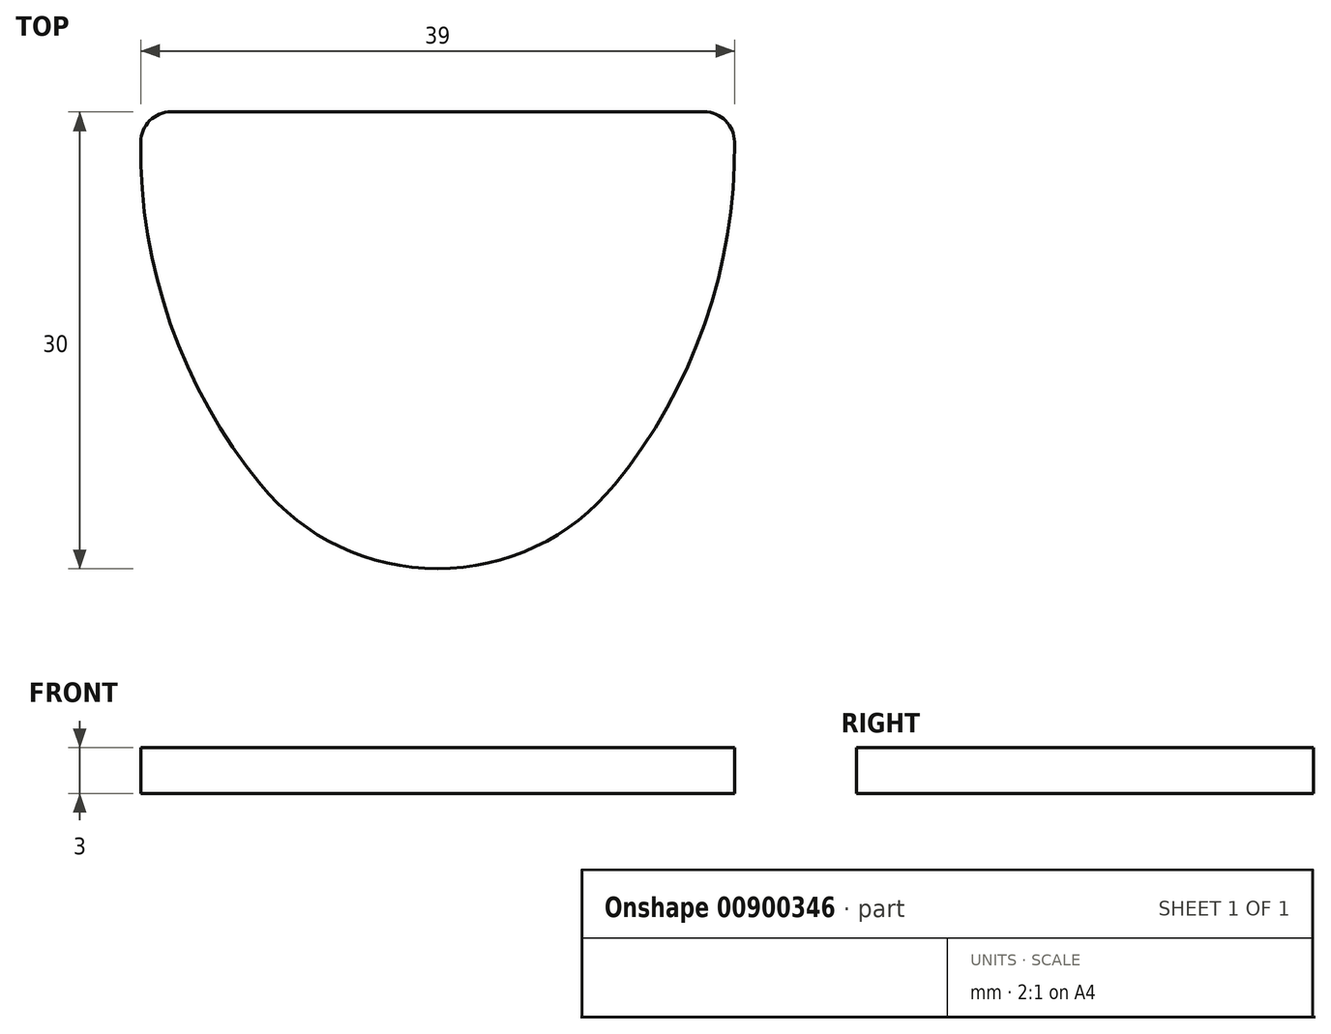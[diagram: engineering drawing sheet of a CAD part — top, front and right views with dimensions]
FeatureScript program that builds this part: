
annotation { "Feature Type Name" : "Feature", "Feature Type Description" : "" }
export const myFeature = defineFeature(function(context is Context, id is Id, definition is map)
    precondition{}
    {
        {
            var Q0;
            Q0=qCreatedBy(makeId("Top.planeOp"),FACE);
            var sketch = newSketch(context, id + "F0", { "sketchPlane" : qUnion([Q0])});
            skLineSegment(sketch, "E0", {"start": v(-17.5, 0) * mm, "end": v(0, 0) * mm});
            skLineSegment(sketch, "E1", {"start": v(0, 0) * mm, "end": v(17.5, 0) * mm});
            skArc(sketch, "E2", {"start": v(11.62, -24.48) * mm, "mid": v(17.54, -13.92) * mm, "end": v(19.5, -1.98) * mm});
            skArc(sketch, "E3", {"start": v(-19.5, -1.98) * mm, "mid": v(-17.54, -13.92) * mm, "end": v(-11.62, -24.48) * mm});
            skArc(sketch, "E4", {"start": v(-11.62, -24.48) * mm, "mid": v(0, -30) * mm, "end": v(11.62, -24.48) * mm});
            skPoint(sketch, "E5.visualSharp", {"position": v(-19.42, 0) * mm});
            skArc(sketch, "E5.filletArc", {"start": v(-17.5, 0) * mm, "mid": v(-18.9, -0.58) * mm, "end": v(-19.5, -1.98) * mm});
            skPoint(sketch, "E6.visualSharp", {"position": v(19.42, 0) * mm});
            skArc(sketch, "E6.filletArc", {"start": v(19.5, -1.98) * mm, "mid": v(18.9, -0.58) * mm, "end": v(17.5, 0) * mm});
            skPoint(sketch, "E7", {"position": v(0, -14) * mm});
            skCircle(sketch, "E8", {"center": v(-17.5, -2) * mm, "radius": 2 * mm, "construction": true});
            skSolve(sketch);
        }
        {
            var Q0;
            Q0=qSketchRegion(id+"F0",true);
            extrude(context, id + "F1", {"entities" : qUnion([Q0]), "depth" : 3 * mm, "offsetDistance" : 25 * mm});
        }
    });
